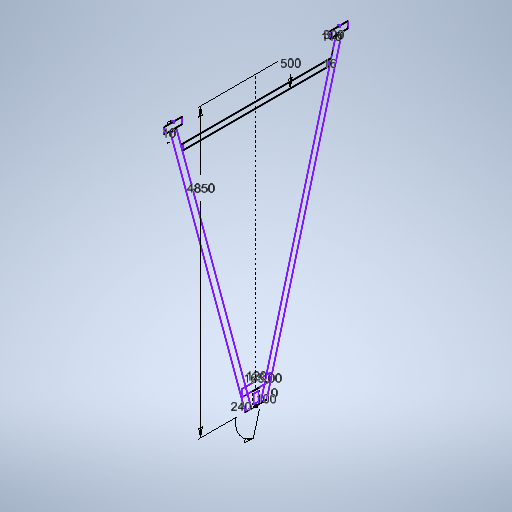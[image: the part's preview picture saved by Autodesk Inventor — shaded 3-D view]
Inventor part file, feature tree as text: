
AUTODESK INVENTOR PART (.ipt)
format: ipt  version: 2025 (Build 290162010, 162A)  size: 282,624 bytes
history: native  units: mm
features: sketch x1
ambient origin geometry x8: Origin, YZ Plane, XZ Plane, XY Plane, X Axis, Y Axis, Z Axis, Center Point
feature tree (1):
  sketch  "Sketch2"  dims[d0=120.0mm d1=240.0mm d2=4850.0mm d3=300.0mm d4=110.0mm d5=100.0mm d7=0.0mm d8=15.0deg d9=16.0mm d10=500.0mm d11=10.0mm]
